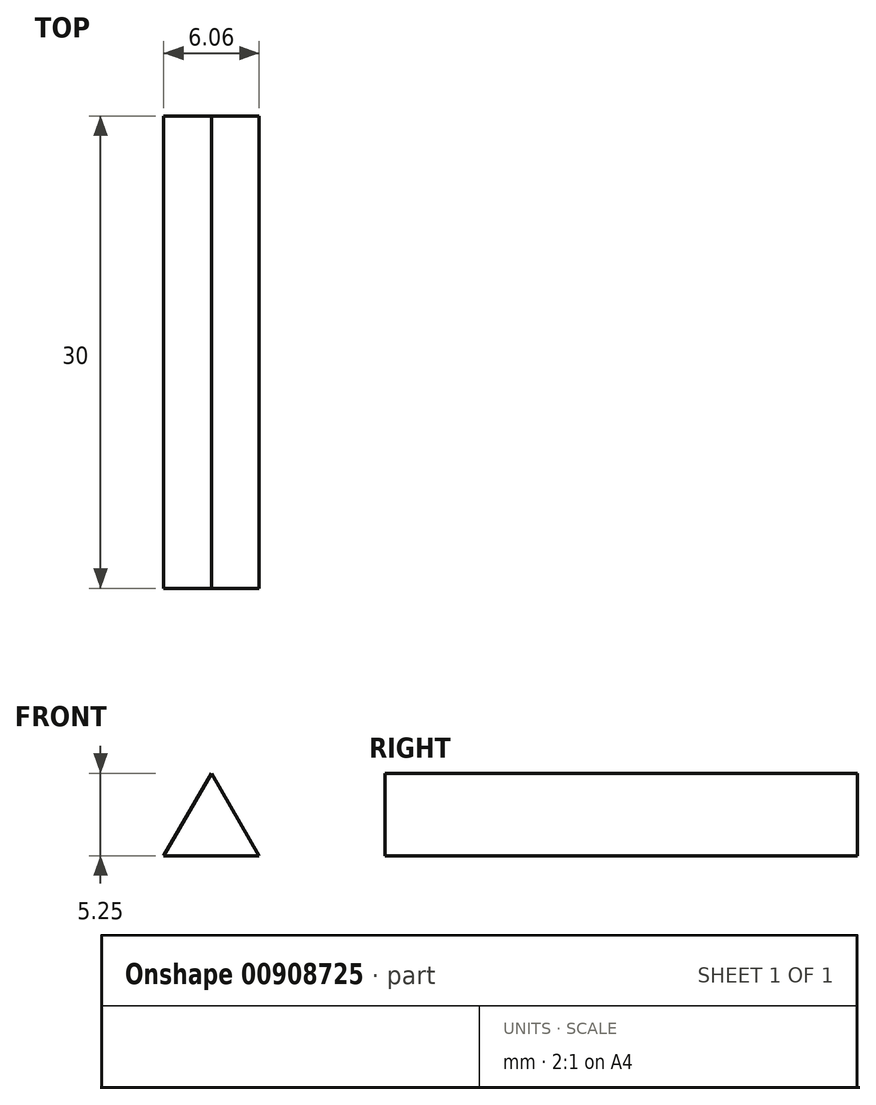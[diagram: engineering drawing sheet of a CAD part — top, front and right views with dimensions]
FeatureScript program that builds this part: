
annotation { "Feature Type Name" : "Feature", "Feature Type Description" : "" }
export const myFeature = defineFeature(function(context is Context, id is Id, definition is map)
    precondition{}
    {
        {
            var Q0;
            Q0=qCreatedBy(makeId("Front.planeOp"),FACE);
            var sketch = newSketch(context, id + "F0", { "sketchPlane" : qUnion([Q0])});
            skLineSegment(sketch, "E0.0", {"start": v(-3.03, -1.75) * mm, "end": v(0, 3.5) * mm});
            skLineSegment(sketch, "E0.1", {"start": v(0, 3.5) * mm, "end": v(3.03, -1.75) * mm});
            skLineSegment(sketch, "E0.2", {"start": v(3.03, -1.75) * mm, "end": v(-3.03, -1.75) * mm});
            skSolve(sketch);
        }
        {
            var Q0;
            Q0=makeQuery(id+"F0.imprint","IMPRINT",FACE,{"disambiguationData":[TD([[makeQuery(id+"F0.imprint","IMPRINT",EDGE,{"derivedFrom":sQuery(id+"F0.wireOp",EDGE,"E0.0")}),-1.0]])]});
            extrude(context, id + "F1", {"entities" : qUnion([Q0]), "depth" : 30 * mm, "offsetDistance" : 25 * mm, "symmetric" : true});
        }
    });
